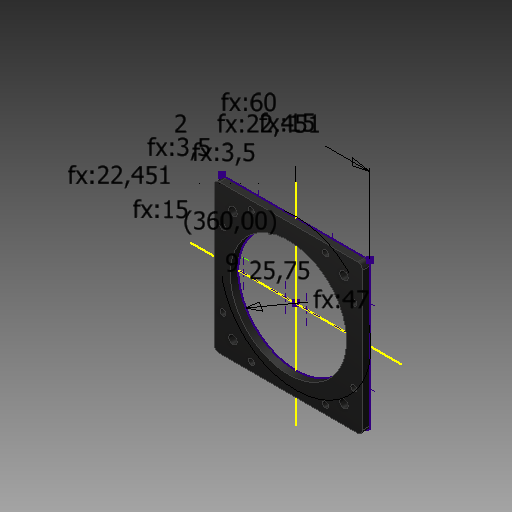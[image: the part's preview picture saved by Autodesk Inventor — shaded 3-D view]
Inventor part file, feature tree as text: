
AUTODESK INVENTOR PART (.ipt)
format: ipt  version: 2019 (Build 230136000, 136)  size: 175,616 bytes
history: native  units: mm
features: other x6, hole x2, extrude x1
ambient origin geometry x8: Origin, YZ Plane, XZ Plane, XY Plane, X Axis, Y Axis, Z Axis, Center Point
bodies: Solid1 (feature_tree)
feature tree (9):
  other  "Table"
  other  "filler_ring-01"
  other  "filler_ring-02"
  other  "filler_ring-03"
  other  "filler_ring-04"
  other  "<userpath>\OneDrive - Van Ierland\Documents\Inventor\FlightSim\Instrument.xlsx"
  extrude  "Extrusion2"  Depth=60.0mm
  hole  "Hole5"  [1 undecoded]
  hole  "Hole6"  [1 undecoded]
note: 2 required parameter values undecoded (feature->parameter linkage not recoverable at this tier; creation-order binding heuristic only, values carry confidence <= 0.55)
